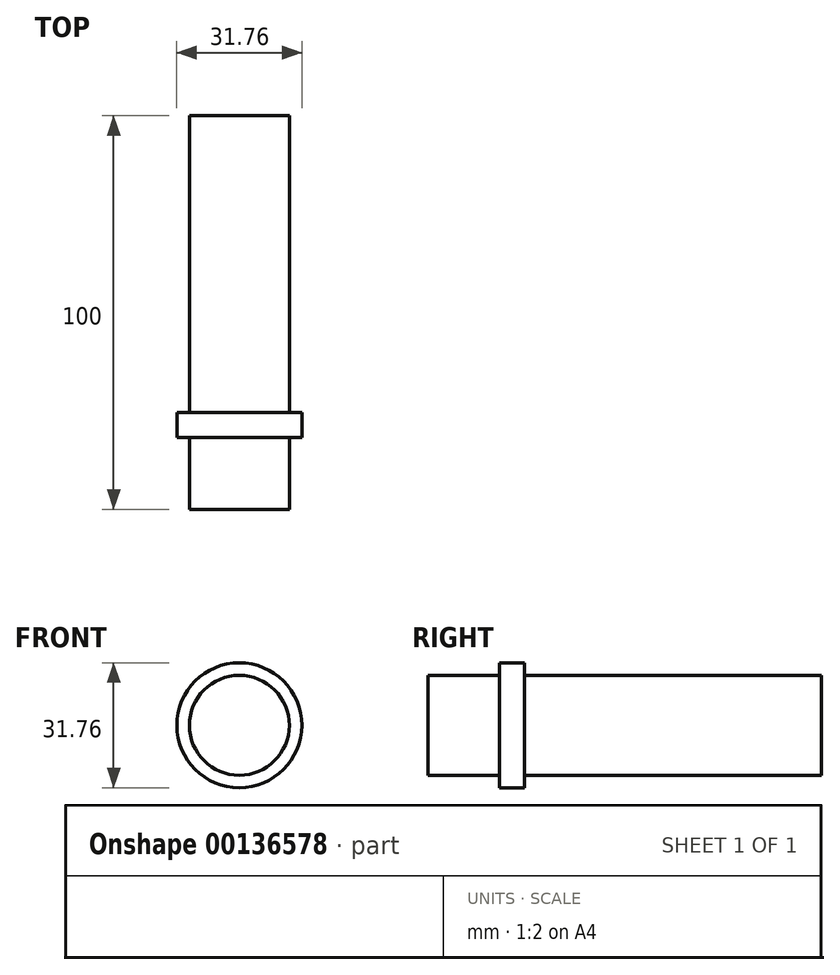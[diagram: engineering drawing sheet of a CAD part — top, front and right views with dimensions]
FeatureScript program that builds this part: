
annotation { "Feature Type Name" : "Feature", "Feature Type Description" : "" }
export const myFeature = defineFeature(function(context is Context, id is Id, definition is map)
    precondition{}
    {
        {
            var Q0;
            Q0=qCreatedBy(makeId("Front.planeOp"),FACE);
            var sketch = newSketch(context, id + "F0", { "sketchPlane" : qUnion([Q0])});
            skCircle(sketch, "E0", {"center": v(0, 0) * mm, "radius": 12.7 * mm});
            skSolve(sketch);
        }
        {
            var Q0;
            Q0=makeQuery(id+"F0.imprint","IMPRINT",FACE,{"disambiguationData":[TD([[makeQuery(id+"F0.imprint","IMPRINT",EDGE,{"derivedFrom":sQuery(id+"F0.wireOp",EDGE,"J4wqMHd1-stYH-uC6Y-AUb4-q8iKy2J3qef3")}),-1.0]])]});
            var Q1;
            Q1=makeQuery(id+"F0.imprint","IMPRINT",FACE,{"disambiguationData":[TD([[makeQuery(id+"F0.imprint","IMPRINT",EDGE,{"derivedFrom":sQuery(id+"F0.wireOp",EDGE,"E0")}),1.0]])]});
            extrude(context, id + "F1", {"entities" : qUnion([Q0, Q1]), "depth" : 25.4 * mm});
        }
        {
            var Q0;
            Q0=makeQuery(id+"F1.opExtrude","CAP_FACE",FACE,{"disambiguationData":[OSD([sQuery(id+"F0.wireOp",EDGE,"J4wqMHd1-stYH-uC6Y-AUb4-q8iKy2J3qef3"),sQuery(id+"F0.wireOp",EDGE,"E0")])],"isStart":false});
            var sketch = newSketch(context, id + "F2", { "sketchPlane" : qUnion([Q0])});
            skCircle(sketch, "E1", {"center": v(0, 0) * mm, "radius": 15.88 * mm});
            skSolve(sketch);
        }
        {
            var Q0;
            Q0=makeQuery(id+"F2.imprint","IMPRINT",FACE,{"disambiguationData":[TD([[makeQuery(id+"F2.imprint","IMPRINT",EDGE,{"derivedFrom":sQuery(id+"F2.wireOp",EDGE,"E1")}),1.0]])]});
            var Q1;
            Q1=makeQuery(id+"F2.imprint","IMPRINT",FACE,{"disambiguationData":[TD([[makeQuery(id+"F2.imprint","IMPRINT",EDGE,{"derivedFrom":makeQuery(id+"F1.opExtrude","CAP_EDGE",EDGE,{"disambiguationData":[OSD([sQuery(id+"F0.wireOp",EDGE,"E0")])],"isStart":false})}),1.0]])]});
            extrude(context, id + "F3", {"entities" : qUnion([Q0, Q1]), "depth" : 6.35 * mm});
        }
        {
            var Q0;
            Q0=makeQuery(id+"F3.opExtrude","CAP_FACE",FACE,{"disambiguationData":[OSD([sQuery(id+"F0.wireOp",EDGE,"E0"),sQuery(id+"F2.wireOp",EDGE,"E1")])],"isStart":false});
            var sketch = newSketch(context, id + "F4", { "sketchPlane" : qUnion([Q0])});
            skCircle(sketch, "E2", {"center": v(0, 0) * mm, "radius": 12.7 * mm});
            skSolve(sketch);
        }
        {
            var Q0;
            Q0=makeQuery(id+"F4.imprint","IMPRINT",FACE,{"disambiguationData":[TD([[makeQuery(id+"F4.imprint","IMPRINT",EDGE,{"derivedFrom":sQuery(id+"F4.wireOp",EDGE,"E2")}),1.0]])]});
            extrude(context, id + "F5", {"entities" : qUnion([Q0]), "operationType" : NewBodyOperationType.ADD, "depth" : 18.25 * mm});
        }
        {
            var Q0;
            Q0=makeQuery(id+"F1.opExtrude","CAP_FACE",FACE,{"disambiguationData":[OSD([sQuery(id+"F0.wireOp",EDGE,"E0")])],"isStart":true});
            extrude(context, id + "F6", {"entities" : qUnion([Q0]), "operationType" : NewBodyOperationType.ADD, "depth" : 50 * mm});
        }
    });
